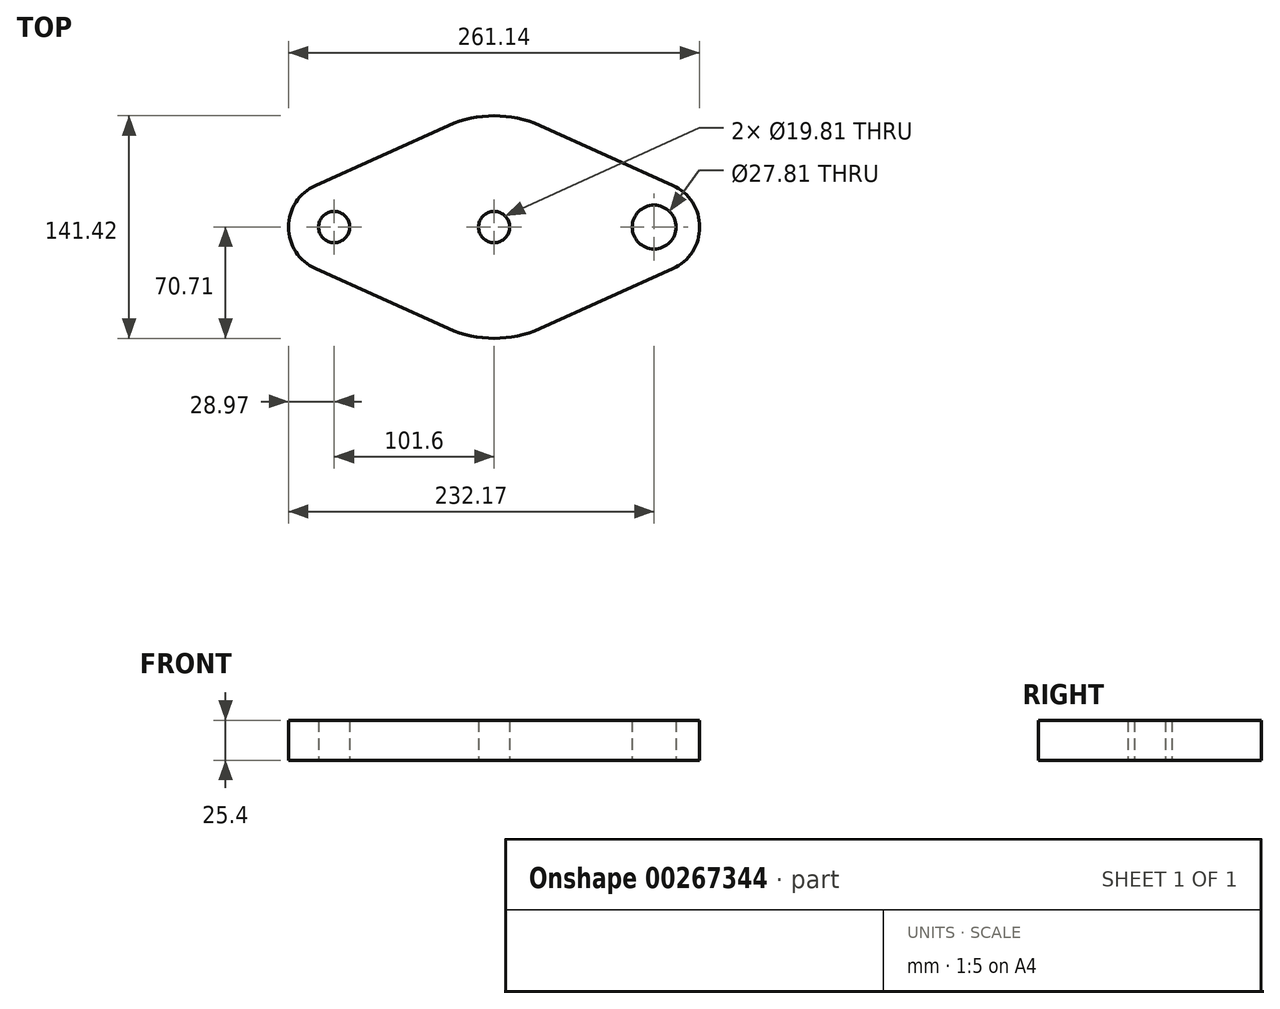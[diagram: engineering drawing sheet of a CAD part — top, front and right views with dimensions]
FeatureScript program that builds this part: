
annotation { "Feature Type Name" : "Feature", "Feature Type Description" : "" }
export const myFeature = defineFeature(function(context is Context, id is Id, definition is map)
    precondition{}
    {
        {
            var Q0;
            Q0=qCreatedBy(makeId("Top.planeOp"),FACE);
            var sketch = newSketch(context, id + "F0", { "sketchPlane" : qUnion([Q0])});
            skCircle(sketch, "E0", {"center": v(0, 0) * mm, "radius": 64.77 * mm});
            skCircle(sketch, "E1", {"center": v(0, 0) * mm, "radius": 70.7 * mm});
            skLineSegment(sketch, "E2", {"start": v(0, 0) * mm, "end": v(-101.6, 0) * mm});
            skCircle(sketch, "E3", {"center": v(-101.6, 0) * mm, "radius": 9.9 * mm});
            skCircle(sketch, "E4", {"center": v(-101.6, 0) * mm, "radius": 13.9 * mm});
            skLineSegment(sketch, "E5.MirrorCS", {"start": v(0, 0) * mm, "end": v(101.6, 0) * mm});
            skCircle(sketch, "E6.MirrorC", {"center": v(101.6, 0) * mm, "radius": 13.9 * mm});
            skCircle(sketch, "E7.MirrorC", {"center": v(101.6, 0) * mm, "radius": 9.9 * mm});
            skCircle(sketch, "E8", {"center": v(-101.6, 0) * mm, "radius": 28.97 * mm});
            skCircle(sketch, "E9.MirrorC", {"center": v(101.6, 0) * mm, "radius": 28.97 * mm});
            skLineSegment(sketch, "E10", {"start": v(-113.5, 26.41) * mm, "end": v(-29.05, 64.46) * mm});
            skLineSegment(sketch, "E11", {"start": v(-113.5, -26.41) * mm, "end": v(-29.05, -64.46) * mm});
            skLineSegment(sketch, "E12.MirrorCS", {"start": v(113.5, 26.41) * mm, "end": v(29.05, 64.46) * mm});
            skLineSegment(sketch, "E13.MirrorCS", {"start": v(113.5, -26.41) * mm, "end": v(29.05, -64.46) * mm});
            skCircle(sketch, "E14", {"center": v(0, 0) * mm, "radius": 9.9 * mm});
            skSolve(sketch);
        }
        {
            var Q0;
            Q0 = qSketchRegion(id + "F0", true);
            var Q1;
            {var subQ0=sQuery(id+"F0.wireOp",EDGE,"E14");var subQ1=sQuery(id+"F0.wireOp",EDGE,"E2");var subQ2=makeQuery(id+"F0.imprint","INTERSECT",VERTEX,{"derivedFrom":[subQ1,subQ0]});Q1=makeQuery(id+"F0.imprint","IMPRINT",FACE,{"disambiguationData":[TD([[makeQuery(id+"F0.imprint","IMPRINT",EDGE,{"disambiguationData":[TD([[subQ2,-1.0]])],"derivedFrom":subQ1}),1.0]])]});}
            var Q2;
            {var subQ0=sQuery(id+"F0.wireOp",EDGE,"E14");var subQ1=sQuery(id+"F0.wireOp",EDGE,"E2");var subQ2=makeQuery(id+"F0.imprint","INTERSECT",VERTEX,{"derivedFrom":[subQ1,subQ0]});Q2=makeQuery(id+"F0.imprint","IMPRINT",FACE,{"disambiguationData":[TD([[makeQuery(id+"F0.imprint","IMPRINT",EDGE,{"disambiguationData":[TD([[subQ2,-1.0]])],"derivedFrom":subQ1}),-1.0]])]});}
            var Q3;
            Q3=makeQuery(id+"F0.imprint","IMPRINT",FACE,{"disambiguationData":[TD([[makeQuery(id+"F0.imprint","IMPRINT",EDGE,{"derivedFrom":sQuery(id+"F0.wireOp",EDGE,"E6.MirrorC")}),-1.0]])]});
            var Q4;
            Q4=makeQuery(id+"F0.imprint","IMPRINT",FACE,{"disambiguationData":[TD([[makeQuery(id+"F0.imprint","IMPRINT",EDGE,{"derivedFrom":sQuery(id+"F0.wireOp",EDGE,"E3")}),-1.0]])]});
            extrude(context, id + "F1", {"entities" : qUnion([Q0, Q1, Q2, Q3, Q4]), "depth" : 25.4 * mm});
        }
    });
